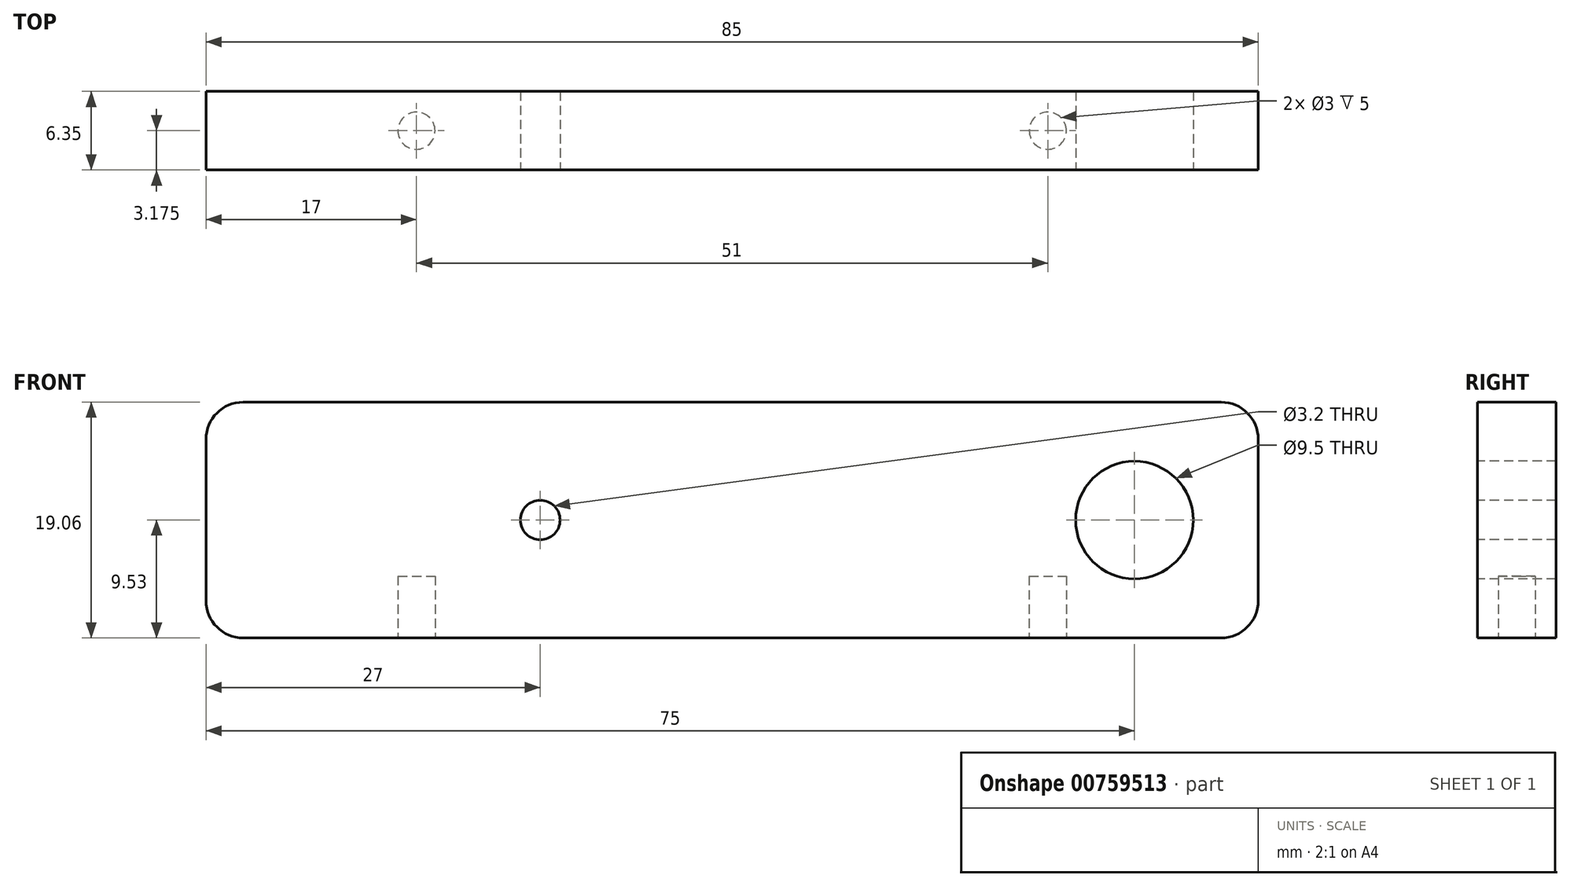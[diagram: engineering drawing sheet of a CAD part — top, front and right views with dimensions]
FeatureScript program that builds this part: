
annotation { "Feature Type Name" : "Feature", "Feature Type Description" : "" }
export const myFeature = defineFeature(function(context is Context, id is Id, definition is map)
    precondition{}
    {
        {
            var Q0;
            Q0=qCreatedBy(makeId("Front.planeOp"),FACE);
            var sketch = newSketch(context, id + "F0", { "sketchPlane" : qUnion([Q0])});
            skLineSegment(sketch, "E0.bottom", {"start": v(-39.5, 9.53) * mm, "end": v(39.5, 9.53) * mm});
            skLineSegment(sketch, "E0.top", {"start": v(-39.5, -9.53) * mm, "end": v(39.5, -9.53) * mm});
            skLineSegment(sketch, "E0.left", {"start": v(-42.5, 6.52) * mm, "end": v(-42.5, -6.53) * mm});
            skLineSegment(sketch, "E0.right", {"start": v(42.5, 6.52) * mm, "end": v(42.5, -6.53) * mm});
            skPoint(sketch, "E0.middle", {"position": v(0, 0) * mm});
            skPoint(sketch, "E1.visualSharp", {"position": v(-42.5, 9.53) * mm});
            skArc(sketch, "E1.filletArc", {"start": v(-39.5, 9.52) * mm, "mid": v(-41.62, 8.65) * mm, "end": v(-42.5, 6.52) * mm});
            skPoint(sketch, "E2.visualSharp", {"position": v(42.5, 9.53) * mm});
            skArc(sketch, "E2.filletArc", {"start": v(42.5, 6.52) * mm, "mid": v(41.62, 8.65) * mm, "end": v(39.5, 9.52) * mm});
            skPoint(sketch, "E3.visualSharp", {"position": v(42.5, -9.53) * mm});
            skArc(sketch, "E3.filletArc", {"start": v(39.5, -9.53) * mm, "mid": v(41.62, -8.65) * mm, "end": v(42.5, -6.53) * mm});
            skPoint(sketch, "E4.visualSharp", {"position": v(-42.5, -9.53) * mm});
            skArc(sketch, "E4.filletArc", {"start": v(-42.5, -6.53) * mm, "mid": v(-41.62, -8.65) * mm, "end": v(-39.5, -9.52) * mm});
            skSolve(sketch);
        }
        {
            var Q0;
            Q0=qCreatedBy(makeId("Front.planeOp"),FACE);
            var sketch = newSketch(context, id + "F1", { "sketchPlane" : qUnion([Q0])});
            skCircle(sketch, "E5", {"center": v(32.5, 0) * mm, "radius": 4.75 * mm});
            skCircle(sketch, "E6", {"center": v(-15.5, 0) * mm, "radius": 1.6 * mm});
            skSolve(sketch);
        }
        {
            var Q0;
            Q0=makeQuery(id+"F0.imprint","IMPRINT",FACE,{"disambiguationData":[TD([[makeQuery(id+"F0.imprint","IMPRINT",EDGE,{"derivedFrom":sQuery(id+"F0.wireOp",EDGE,"E0.bottom")}),-1.0]])]});
            var Q1;
            Q1=sQuery(id+"F1.wireOp",EDGE,"E6");
            var Q2;
            Q2=sQuery(id+"F0.wireOp",EDGE,"E0.bottom");
            var Q3;
            Q3=sQuery(id+"F1.wireOp",EDGE,"E5");
            var Q4;
            Q4=sQuery(id+"F0.wireOp",EDGE,"E2.filletArc");
            var Q5;
            Q5=sQuery(id+"F0.wireOp",EDGE,"E0.right");
            var Q6;
            Q6=sQuery(id+"F0.wireOp",EDGE,"E3.filletArc");
            var Q7;
            Q7=sQuery(id+"F0.wireOp",EDGE,"E0.top");
            var Q8;
            Q8=sQuery(id+"F0.wireOp",EDGE,"E1.filletArc");
            var Q9;
            Q9=sQuery(id+"F0.wireOp",EDGE,"E0.left");
            var Q10;
            Q10=sQuery(id+"F0.wireOp",EDGE,"E4.filletArc");
            extrude(context, id + "F2", {"entities" : qUnion([Q0]), "surfaceOperationType" : NewSurfaceOperationType.ADD, "surfaceEntities" : qUnion([Q1, Q2, Q3, Q4, Q5, Q6, Q7, Q8, Q9, Q10]), "oppositeDirection" : true, "depth" : 6.35 * mm, "offsetDistance" : 25 * mm});
        }
        {
            var Q0;
            Q0 = qSketchRegion(id + "F1", true);
            extrude(context, id + "F3", {"entities" : qUnion([Q0]), "operationType" : NewBodyOperationType.REMOVE, "oppositeDirection" : true, "depth" : 25 * mm, "offsetDistance" : 25 * mm});
        }
        {
            var Q0;
            Q0=qCreatedBy(makeId("Top.planeOp"),FACE);
            var sketch = newSketch(context, id + "F4", { "sketchPlane" : qUnion([Q0])});
            skCircle(sketch, "E7", {"center": v(-25.5, 3.17) * mm, "radius": 1.5 * mm});
            skCircle(sketch, "E8", {"center": v(25.5, 3.17) * mm, "radius": 1.5 * mm});
            skSolve(sketch);
        }
        {
            var Q0;
            Q0=makeQuery(id+"F2.opExtrude","SWEPT_FACE",FACE,{"disambiguationData":[OSD([sQuery(id+"F0.wireOp",EDGE,"E0.top")])]});
            var sketch = newSketch(context, id + "F5", { "sketchPlane" : qUnion([Q0])});
            skCircle(sketch, "E9.0", {"center": v(-25.5, -3.17) * mm, "radius": 1.5 * mm});
            skCircle(sketch, "E10.0", {"center": v(25.5, -3.17) * mm, "radius": 1.5 * mm});
            skSolve(sketch);
        }
        {
            var Q0;
            Q0 = qSketchRegion(id + "F5", true);
            extrude(context, id + "F6", {"entities" : qUnion([Q0]), "operationType" : NewBodyOperationType.REMOVE, "oppositeDirection" : true, "depth" : 5 * mm, "offsetDistance" : 25 * mm});
        }
    });
